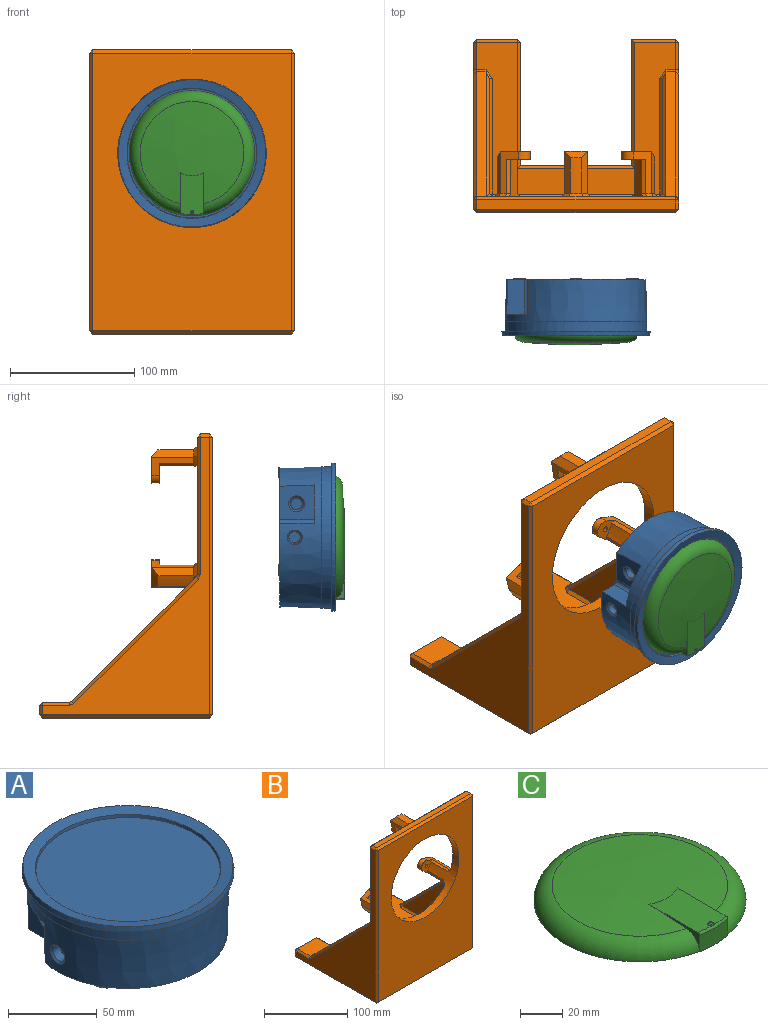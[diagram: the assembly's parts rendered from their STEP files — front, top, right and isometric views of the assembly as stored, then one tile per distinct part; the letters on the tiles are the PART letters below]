
ASSEMBLY  parts=3 mates=2
PART A: 42 faces, bbox 119.6x119.6x45.6 mm
  f0: cone r=4.75mm half-angle=2.5deg, axis (-1,0,0), area 154.8mm2, adj f1,f41
  f1: cone r=6.35mm half-angle=45deg, axis (-1,0,0), area 56.8mm2, adj f0,f20
  f2: cone r=6.35mm half-angle=45deg, axis (-1,0,0), area 78.9mm2, adj f3,f21
  f3: cone r=4.75mm half-angle=2.5deg, axis (-1,0,0), area 154.8mm2, adj f2,f40
  f4: cone r=6.35mm half-angle=45deg, axis (0,0,-1), area 78.9mm2, adj f5,f22
  f5: cone r=4.75mm half-angle=2.5deg, axis (0,0,-1), area 154.8mm2, adj f4,f39
  f6: cone r=6.34mm half-angle=45deg, axis (0,0,-1), area 78.8mm2, adj f7,f22
  f7: cone r=4.74mm half-angle=2.4deg, axis (0,0,-1), area 154.6mm2, adj f6,f38
  f8: cylinder r=1.65mm len=6.83mm, axis (0,0,1), area 70.9mm2, adj f9,f37
  f9: cone r=2.44mm half-angle=45deg, axis (0,0,-1), area 14.3mm2, adj f8,f23
  f10: cylinder r=1.65mm len=6.83mm, axis (0,0,1), area 70.9mm2, adj f11,f36
  f11: cone r=2.44mm half-angle=45deg, axis (0,0,-1), area 14.3mm2, adj f10,f24
  f12: cylinder r=1.65mm len=6.83mm, axis (0,0,1), area 70.9mm2, adj f13,f35
  f13: cone r=2.44mm half-angle=45deg, axis (0,0,-1), area 14.3mm2, adj f12,f25
  f14: cylinder r=4.57mm len=9.14mm, axis (0,0,1), area 14.4mm2, adj f22,f23,f32
  f15: cylinder r=4.57mm len=9.14mm, axis (0,0,1), area 14.4mm2, adj f22,f25,f31
  f16: cone r=52.33mm half-angle=10deg, axis (0,0,1), area 634mm2, adj f17,f27
  f17: cone r=59.26mm half-angle=79.6deg, axis (0,0,1), area 2469mm2, adj f16,f18
  f18: cone r=59.82mm half-angle=10deg, axis (0,0,-1), area 1206mm2, adj f17,f26
  f19: cylinder r=56.96mm len=113.92mm, axis (0,0,1), area 2836.2mm2, adj f20,f26
  f20: cone r=56.07mm half-angle=1.5deg, axis (0,0,1), area 10909.1mm2, adj f1,f19,f21,f22,f28,f29,f31,f32
  f21: plane 27.83x27.77mm, normal (-1,0,0), area 632.2mm2, adj f2,f20,f22,f28,f30
  f22: plane 112.15x112.08mm, normal (0,0,-1), area 9124.6mm2, adj f4,f6,f14,f15,f20,f21,f29,f30
  f23: plane 9.14x9.1mm, normal (0,0,-1), area 43.6mm2, adj f9,f14,f32
  f24: plane 9.14x9.1mm, normal (0,0,-1), area 43.6mm2, adj f11,f33,f34
  f25: plane 9.14x8.26mm, normal (0,0,-1), area 43.6mm2, adj f13,f15,f31
  f26: plane 119.63x119.63mm, normal (0,0,-1), area 1048.3mm2, adj f18,f19
  f27: plane 103.99x103.99mm, normal (0,0,1), area 8492.8mm2, adj f16
  f28: plane 31x17.6mm, normal (0,0,-1), area 339.2mm2, adj f20,f21,f29,f30
  f29: plane 27.76x14.43mm, normal (0,1,0), area 390.2mm2, adj f20,f22,f28,f30
  f30: cylinder r=3.17mm len=27.76mm, axis (0,0,1), area 138.5mm2, adj f21,f22,f28,f29
  f31: cylinder r=56.07mm len=5.6mm, axis (0,0,1), area 3.6mm2, adj f15,f20,f25
  f32: cylinder r=56.07mm len=4.85mm, axis (0,0,1), area 3.6mm2, adj f14,f20,f23
  f33: cylinder r=56.07mm len=4.85mm, axis (0,0,1), area 3.6mm2, adj f20,f24,f34
  f34: cylinder r=4.57mm len=9.14mm, axis (0,0,1), area 14.4mm2, adj f22,f24,f33
  f35: plane 3.3x3.3mm, normal (0,0,-1), area 8.6mm2, adj f12
  f36: plane 3.3x3.3mm, normal (0,0,-1), area 8.6mm2, adj f10
  f37: plane 3.3x3.3mm, normal (0,0,-1), area 8.6mm2, adj f8
  f38: plane 9.04x9.04mm, normal (0,0,-1), area 64.2mm2, adj f7
  f39: plane 9.04x9.04mm, normal (0,0,-1), area 64.2mm2, adj f5
  f40: plane 9.04x9.04mm, normal (-1,0,0), area 64.2mm2, adj f3
  f41: plane 9.04x9.04mm, normal (-1,0,0), area 64.2mm2, adj f0
PART B: 138 faces, bbox 165.1x139.7x228.6 mm
  f0: plane 210.82x160.02mm, normal (0,1,0), area 19012.3mm2, adj f47,f48,f49,f51,f54,f55,f60,f61
  f1: plane 160.02x121.92mm, normal (0,0,1), area 7454.9mm2, adj f79,f82,f83,f90,f91,f101,f102,f107
  f2: plane 223.52x134.62mm, normal (1,0,0), area 7987.7mm2, adj f98,f106,f114,f115,f122,f126,f127,f133
  f3: plane 160.02x7.62mm, normal (0,0,1), area 1219.4mm2, adj f96,f97,f113,f114
  f4: plane 223.52x134.62mm, normal (-1,0,0), area 7987.7mm2, adj f84,f85,f87,f88,f91,f96,f103,f111
  f5: plane 160.02x134.62mm, normal (0,0,-1), area 11993.5mm2, adj f111,f119,f125,f129,f132,f133,f135,f137
  f6: plane 223.52x160.02mm, normal (0,-1,0), area 25277.6mm2, adj f16,f112,f113,f125,f126
  f7: plane 35.56x7.62mm, normal (0,1,0), area 271mm2, adj f8,f128,f134,f137
  f8: plane 101.6x7.62mm, normal (-1,0,0), area 774.2mm2, adj f7,f9,f123,f135
  f9: plane 88.9x7.62mm, normal (0,1,0), area 677.4mm2, adj f8,f10,f117,f132
  f10: plane 99.06x7.62mm, normal (1,0,0), area 754.8mm2, adj f9,f108,f118,f129
  f11: plane 33.02x7.62mm, normal (0,1,0), area 251.6mm2, adj f102,f103,f118,f119
  f12: plane 100.11x100.11mm, normal (0,0.71,0.71), area 1078.8mm2, adj f99,f100,f115,f116
  f13: plane 92.93x92.93mm, normal (-1,0,0), area 4317.8mm2, adj f89,f100,f101
  f14: plane 100.11x100.11mm, normal (0,0.71,0.71), area 1078.8mm2, adj f77,f80,f83,f84
  f15: plane 92.93x92.93mm, normal (1,0,0), area 4317.8mm2, adj f77,f81,f82
  f16: cylinder r=57.79mm len=115.57mm, axis (0,-1,0), area 4926.5mm2, adj f6,f20,f32,f42,f50,f52,f53,f55
  f17: plane 33.97x14.89mm, normal (0.99,0,-0.14), area 231.9mm2, adj f20,f21,f22,f24,f49,f50
  f18: plane 33.97x14.89mm, normal (-0.99,0,-0.14), area 231.9mm2, adj f20,f21,f22,f26,f53,f54
  f19: cylinder r=70.48mm len=28.89mm, axis (0,-1,0), area 272.5mm2, adj f24,f25,f26,f48
  f20: plane 17.38x16.26mm, normal (0,-1,0), area 183.1mm2, adj f16,f17,f18,f21,f23,f50,f53
  f21: cylinder r=7.31mm len=14.46mm, axis (0,-1,0), area 132.4mm2, adj f17,f18,f20,f22
  f22: plane 22.02x18.8mm, normal (0,1,0), area 312.8mm2, adj f17,f18,f21,f23,f24,f25,f26
  f23: cylinder r=2.22mm len=6.35mm, axis (0,-1,0), area 88.7mm2, adj f20,f22
  f24: plane 33.97x5.8mm, normal (0.78,0,0.63), area 235.4mm2, adj f17,f19,f22,f25,f47
  f25: cone r=65.41mm half-angle=45deg, axis (0,-1,0), area 99.9mm2, adj f19,f22,f24,f26
  f26: plane 33.97x5.8mm, normal (-0.78,0,0.63), area 235.4mm2, adj f18,f19,f22,f25,f51
  f27: plane 33.97x11.81mm, normal (-0.62,0,-0.78), area 231.9mm2, adj f30,f31,f32,f34,f69,f70
  f28: plane 33.97x13.98mm, normal (0.37,0,0.93), area 231.9mm2, adj f30,f31,f32,f36,f56,f61
  f29: cylinder r=70.48mm len=28.89mm, axis (0,-1,0), area 272.5mm2, adj f34,f35,f36,f65
  f30: cylinder r=7.31mm len=13.04mm, axis (0,-1,0), area 132.4mm2, adj f27,f28,f31,f32
  f31: plane 24.09x22.36mm, normal (0,1,0), area 312.8mm2, adj f27,f28,f30,f33,f34,f35,f36
  f32: plane 19.4x19.31mm, normal (0,-1,0), area 183.1mm2, adj f16,f27,f28,f30,f33,f56,f70
  f33: cylinder r=2.22mm len=6.35mm, axis (0,-1,0), area 88.7mm2, adj f31,f32
  f34: plane 33.97x7.37mm, normal (0.16,0,-0.99), area 235.4mm2, adj f27,f29,f31,f35,f67
  f35: cone r=65.41mm half-angle=45deg, axis (0,-1,0), area 99.9mm2, adj f29,f31,f34,f36
  f36: plane 33.97x6.96mm, normal (0.93,0,0.36), area 235.4mm2, adj f28,f29,f31,f35,f63
  f37: plane 33.97x13.98mm, normal (-0.37,0,0.93), area 231.9mm2, adj f40,f41,f42,f44,f59,f64
  f38: plane 33.97x11.81mm, normal (0.62,0,-0.78), area 231.9mm2, adj f40,f41,f42,f46,f73,f76
  f39: cylinder r=70.48mm len=28.89mm, axis (0,-1,0), area 272.5mm2, adj f44,f45,f46,f68
  f40: cylinder r=7.31mm len=13.04mm, axis (0,-1,0), area 132.4mm2, adj f37,f38,f41,f42
  f41: plane 24.09x22.36mm, normal (0,1,0), area 312.8mm2, adj f37,f38,f40,f43,f44,f45,f46
  f42: plane 19.4x19.31mm, normal (0,-1,0), area 183.1mm2, adj f16,f37,f38,f40,f43,f59,f76
  f43: cylinder r=2.22mm len=6.35mm, axis (0,-1,0), area 88.7mm2, adj f41,f42
  f44: plane 33.97x6.96mm, normal (-0.93,0,0.36), area 235.4mm2, adj f37,f39,f41,f45,f66
  f45: cone r=65.41mm half-angle=45deg, axis (0,-1,0), area 99.9mm2, adj f39,f41,f44,f46
  f46: plane 33.97x7.37mm, normal (-0.16,0,-0.99), area 235.4mm2, adj f38,f39,f41,f45,f71
  f47: plane 8.27x7.38mm, normal (0.55,0.71,0.44), area 30.8mm2, adj f0,f24,f48,f49
  f48: cone r=70.48mm half-angle=45deg, axis (0,-1,0), area 38.5mm2, adj f0,f19,f47,f51
  f49: plane 5.98x3.39mm, normal (0.7,0.71,-0.1), area 19.7mm2, adj f0,f17,f47,f52
  f50: plane 27.62x2.77mm, normal (0.61,0,-0.79), area 97.1mm2, adj f16,f17,f20,f52
  f51: plane 8.27x7.38mm, normal (-0.55,0.71,0.44), area 30.8mm2, adj f0,f26,f48,f54
  f52: bspline ~5.29x5.08mm, area 16.2mm2, adj f16,f49,f50,f55
  f53: plane 27.62x2.77mm, normal (-0.61,0,-0.79), area 97.1mm2, adj f16,f18,f20,f57
  f54: plane 5.98x3.39mm, normal (-0.7,0.71,-0.1), area 19.7mm2, adj f0,f18,f51,f57
  f55: cone r=60.32mm half-angle=45deg, axis (0,1,0), area 365mm2, adj f0,f16,f52,f58
  f56: plane 27.62x3.26mm, normal (-0.38,0,0.93), area 97.1mm2, adj f16,f28,f32,f58
  f57: bspline ~5.29x5.08mm, area 16.2mm2, adj f16,f53,f54,f60
  f58: bspline ~5.08x4.52mm, area 16.2mm2, adj f16,f55,f56,f61
  f59: plane 27.62x3.26mm, normal (0.38,0,0.93), area 97.1mm2, adj f16,f37,f42,f62
  f60: cone r=60.32mm half-angle=45deg, axis (0,1,0), area 365mm2, adj f0,f16,f57,f62
  f61: plane 6.56x4.19mm, normal (0.26,0.71,0.66), area 19.7mm2, adj f0,f28,f58,f63
  f62: bspline ~5.08x4.52mm, area 16.2mm2, adj f16,f59,f60,f64
  f63: plane 9.04x5.46mm, normal (0.66,0.71,0.25), area 30.8mm2, adj f0,f36,f61,f65
  f64: plane 6.56x4.19mm, normal (-0.26,0.71,0.66), area 19.7mm2, adj f0,f37,f62,f66
  f65: cone r=70.48mm half-angle=45deg, axis (0,-1,0), area 38.5mm2, adj f0,f29,f63,f67
  f66: plane 9.04x5.46mm, normal (-0.66,0.71,0.25), area 30.8mm2, adj f0,f44,f64,f68
  f67: plane 9.56x3.86mm, normal (0.11,0.71,-0.7), area 30.8mm2, adj f0,f34,f65,f69
  f68: cone r=70.48mm half-angle=45deg, axis (0,-1,0), area 38.5mm2, adj f0,f39,f66,f71
  f69: plane 5.74x5.45mm, normal (-0.44,0.71,-0.56), area 19.7mm2, adj f0,f27,f67,f72
  f70: plane 27.62x3.48mm, normal (-0.99,0,-0.14), area 97.1mm2, adj f16,f27,f32,f72
  f71: plane 9.56x3.86mm, normal (-0.11,0.71,-0.7), area 30.8mm2, adj f0,f46,f68,f73
  f72: bspline ~5.48x5.08mm, area 16.2mm2, adj f16,f69,f70,f74
  f73: plane 5.74x5.45mm, normal (0.44,0.71,-0.56), area 19.7mm2, adj f0,f38,f71,f75
  f74: cone r=60.32mm half-angle=45deg, axis (0,1,0), area 365mm2, adj f0,f16,f72,f75
  f75: bspline ~5.48x5.08mm, area 16.2mm2, adj f16,f73,f74,f76
  f76: plane 27.62x3.48mm, normal (0.99,0,-0.14), area 97.1mm2, adj f16,f38,f42,f75
  f77: plane 100.11x100.11mm, normal (0.71,0.5,0.5), area 490.3mm2, adj f14,f15,f78,f79
  f78: bspline ~7.18x5.08mm, area 16.7mm2, adj f0,f77,f80,f81
  f79: bspline ~7.18x5.08mm, area 16.7mm2, adj f1,f77,f82,f83
  f80: plane 7.62x1.8mm, normal (0,0.92,0.38), area 14.8mm2, adj f0,f14,f78,f85
  f81: plane 92.93x2.54mm, normal (0.71,0.71,0), area 333.8mm2, adj f0,f15,f78,f86
  f82: plane 92.93x2.54mm, normal (0.71,0,0.71), area 333.8mm2, adj f1,f15,f79,f86
  f83: plane 7.62x1.8mm, normal (0,0.38,0.92), area 14.8mm2, adj f1,f14,f79,f87
  f84: plane 101.91x101.91mm, normal (-0.71,0.5,0.5), area 508.6mm2, adj f4,f14,f85,f87
  f85: plane 3.59x3.28mm, normal (-0.68,0.68,0.28), area 10.1mm2, adj f4,f80,f84,f88
  f86: plane 2.54x2.54mm, normal (0.58,0.58,0.58), area 5.6mm2, adj f81,f82,f90
  f87: plane 3.59x3.28mm, normal (-0.68,0.28,0.68), area 10.1mm2, adj f4,f83,f84,f91
  f88: plane 110.71x2.54mm, normal (-0.71,0.71,0), area 397.7mm2, adj f0,f4,f85,f92
  f89: plane 92.93x2.54mm, normal (-0.71,0.71,0), area 333.8mm2, adj f0,f13,f93,f94
  f90: plane 134.62x2.54mm, normal (0,0.71,0.71), area 483.6mm2, adj f0,f1,f86,f94
  f91: plane 21.81x2.54mm, normal (-0.71,0,0.71), area 78.3mm2, adj f1,f4,f87,f95
  f92: plane 2.54x2.54mm, normal (-0.58,0.58,0.58), area 5.6mm2, adj f88,f96,f97
  f93: bspline ~7.18x5.08mm, area 16.7mm2, adj f0,f89,f99,f100
  f94: plane 2.54x2.54mm, normal (-0.58,0.58,0.58), area 5.6mm2, adj f89,f90,f101
  f95: plane 2.54x2.54mm, normal (-0.58,0.58,0.58), area 5.6mm2, adj f91,f102,f103
  f96: plane 7.62x2.54mm, normal (-0.71,0,0.71), area 27.4mm2, adj f3,f4,f92,f104
  f97: plane 160.02x2.54mm, normal (0,0.71,0.71), area 574.8mm2, adj f0,f3,f92,f105
  f98: plane 110.71x2.54mm, normal (0.71,0.71,0), area 397.7mm2, adj f0,f2,f105,f106
  f99: plane 7.62x1.8mm, normal (0,0.92,0.38), area 14.8mm2, adj f0,f12,f93,f106
  f100: plane 100.11x100.11mm, normal (-0.71,0.5,0.5), area 490.3mm2, adj f12,f13,f93,f107
  f101: plane 92.93x2.54mm, normal (-0.71,0,0.71), area 333.8mm2, adj f1,f13,f94,f107
  f102: plane 33.02x2.54mm, normal (0,0.71,0.71), area 118.6mm2, adj f1,f11,f95,f109
  f103: plane 7.62x2.54mm, normal (-0.71,0.71,0), area 27.4mm2, adj f4,f11,f95,f110
  f104: plane 2.54x2.54mm, normal (-0.58,-0.58,0.58), area 5.6mm2, adj f96,f112,f113
  f105: plane 2.54x2.54mm, normal (0.58,0.58,0.58), area 5.6mm2, adj f97,f98,f114
  f106: plane 3.59x3.28mm, normal (0.68,0.68,0.28), area 10.1mm2, adj f2,f98,f99,f115
  f107: bspline ~7.18x5.08mm, area 16.7mm2, adj f1,f100,f101,f116
  f108: plane 101.6x2.54mm, normal (0.71,0,0.71), area 360.4mm2, adj f1,f10,f109,f117
  f109: plane 2.54x2.54mm, normal (0.58,0.58,0.58), area 5.6mm2, adj f102,f108,f118
  f110: plane 2.54x2.54mm, normal (-0.58,0.58,-0.58), area 5.6mm2, adj f103,f111,f119
  f111: plane 134.62x2.54mm, normal (-0.71,0,-0.71), area 483.6mm2, adj f4,f5,f110,f120
  f112: plane 223.52x2.54mm, normal (-0.71,-0.71,0), area 802.9mm2, adj f4,f6,f104,f120
  f113: plane 160.02x2.54mm, normal (0,-0.71,0.71), area 574.8mm2, adj f3,f6,f104,f121
  f114: plane 7.62x2.54mm, normal (0.71,0,0.71), area 27.4mm2, adj f2,f3,f105,f121
  f115: plane 101.91x101.91mm, normal (0.71,0.5,0.5), area 508.6mm2, adj f2,f12,f106,f122
  f116: plane 7.62x1.8mm, normal (0,0.38,0.92), area 14.8mm2, adj f1,f12,f107,f122
  f117: plane 93.98x2.54mm, normal (0,0.71,0.71), area 328.5mm2, adj f1,f9,f108,f123
  f118: plane 7.62x2.54mm, normal (0.71,0.71,0), area 27.4mm2, adj f10,f11,f109,f124
  f119: plane 33.02x2.54mm, normal (0,0.71,-0.71), area 118.6mm2, adj f5,f11,f110,f124
  f120: plane 2.54x2.54mm, normal (-0.58,-0.58,-0.58), area 5.6mm2, adj f111,f112,f125
  f121: plane 2.54x2.54mm, normal (0.58,-0.58,0.58), area 5.6mm2, adj f113,f114,f126
  f122: plane 3.59x3.28mm, normal (0.68,0.28,0.68), area 10.1mm2, adj f2,f115,f116,f127
  f123: plane 104.14x2.54mm, normal (-0.71,0,0.71), area 365mm2, adj f1,f8,f117,f128
  f124: plane 2.54x2.54mm, normal (0.58,0.58,-0.58), area 5.6mm2, adj f118,f119,f129
  f125: plane 160.02x2.54mm, normal (0,-0.71,-0.71), area 574.8mm2, adj f5,f6,f120,f130
  f126: plane 223.52x2.54mm, normal (0.71,-0.71,0), area 802.9mm2, adj f2,f6,f121,f130
  f127: plane 21.81x2.54mm, normal (0.71,0,0.71), area 78.3mm2, adj f1,f2,f122,f131
  f128: plane 35.56x2.54mm, normal (0,0.71,0.71), area 123.2mm2, adj f1,f7,f123,f131
  f129: plane 101.6x2.54mm, normal (0.71,0,-0.71), area 360.4mm2, adj f5,f10,f124,f132
  f130: plane 2.54x2.54mm, normal (0.58,-0.58,-0.58), area 5.6mm2, adj f125,f126,f133
  f131: plane 2.54x2.54mm, normal (0.58,0.58,0.58), area 5.6mm2, adj f127,f128,f134
  f132: plane 93.98x2.54mm, normal (0,0.71,-0.71), area 328.5mm2, adj f5,f9,f129,f135
  f133: plane 134.62x2.54mm, normal (0.71,0,-0.71), area 483.6mm2, adj f2,f5,f130,f136
  f134: plane 7.62x2.54mm, normal (0.71,0.71,0), area 27.4mm2, adj f2,f7,f131,f136
  f135: plane 104.14x2.54mm, normal (-0.71,0,-0.71), area 365mm2, adj f5,f8,f132,f137
  f136: plane 2.54x2.54mm, normal (0.58,0.58,-0.58), area 5.6mm2, adj f133,f134,f137
  f137: plane 35.56x2.54mm, normal (0,0.71,-0.71), area 123.2mm2, adj f5,f7,f135,f136
PART C: 24 faces, bbox 109.2x108.2x11.5 mm
  f0: cylinder r=0.13mm len=0.51mm, axis (0,0,1), area 0.4mm2, adj f16,f17,f20
  f1: cylinder r=1.27mm len=2.54mm, axis (0,0,1), area 5.6mm2, adj f15,f16,f17,f19,f20,f21
  f2: cylinder r=1.52mm len=3.05mm, axis (0,0,1), area 10.3mm2, adj f5,f15
  f3: sphere r=457.2mm, area 5026.8mm2, adj f4,f5,f6,f7
  f4: torus R=40.88mm, axis (0,0,-1), area 3738.1mm2, adj f3,f6,f7,f8
  f5: plane 33.85x19.05mm, normal (0,0,1), area 596.6mm2, adj f2,f3,f6,f7,f14
  f6: plane 34.18x10.53mm, normal (1,0,0), area 49.4mm2, adj f3,f4,f5,f13,f14
  f7: plane 34.18x10.53mm, normal (-1,0,0), area 49.4mm2, adj f3,f4,f5,f13,f14
  f8: plane 100.78x99.87mm, normal (0,0,-1), area 7022.3mm2, adj f4,f10,f11,f12
  f9: plane 50.39x19.05mm, normal (0,0,-1), area 954.1mm2, adj f10,f11,f12,f13
  f10: plane 19.05x0.28mm, normal (0,1,0), area 5.4mm2, adj f8,f9,f11,f12
  f11: plane 49.48x0.28mm, normal (1,0,0), area 14mm2, adj f8,f9,f10,f13
  f12: plane 49.48x0.28mm, normal (-1,0,0), area 14mm2, adj f8,f9,f10,f13
  f13: cylinder r=50.39mm len=19.05mm, axis (0,0,1), area 183.5mm2, adj f6,f7,f9,f11,f12,f14
  f14: torus R=49.25mm, axis (0,0,-1), area 34.5mm2, adj f5,f6,f7,f13
  f15: plane 3.05x3.05mm, normal (0,0,1), area 2.2mm2, adj f1,f2,f19,f21,f22,f23
  f16: plane 2.54x2.54mm, normal (0,0,1), area 5mm2, adj f0,f1
  f17: plane 1.27x0.25mm, normal (0,0,-1), area 0.3mm2, adj f0,f1,f19,f21
  f18: plane 2.79x0.25mm, normal (0,0,1), area 0.7mm2, adj f19,f21,f22,f23
  f19: plane 2.79x0.67mm, normal (0,1,0), area 1.8mm2, adj f1,f15,f17,f18,f20,f22,f23
  f20: plane 1.27x0.25mm, normal (0,0,-1), area 0.3mm2, adj f0,f1,f19,f21
  f21: plane 2.79x0.67mm, normal (0,-1,0), area 1.8mm2, adj f1,f15,f17,f18,f20,f22,f23
  f22: plane 0.46x0.25mm, normal (1,0,0), area 0.1mm2, adj f15,f18,f19,f21
  f23: plane 0.46x0.25mm, normal (-1,0,0), area 0.1mm2, adj f15,f18,f19,f21
PLACE A rot(axis=(1,0,0),90deg) t=(-7.03,-131.89,86.38)mm
PLACE B t=(-7.03,-31.49,-59.03)mm fixed
PLACE C rot(axis=(1,0,0),90deg) t=(-7.03,-129.98,86.38)mm
MATE fastened C.f4 <-> A.f16  axis (0,1,0) through (-7.03,-139.81,86.38)mm
MATE slider A.f16 <-> B.f16  axis (0,-1,0) through (-7.03,-98.03,86.38)mm
